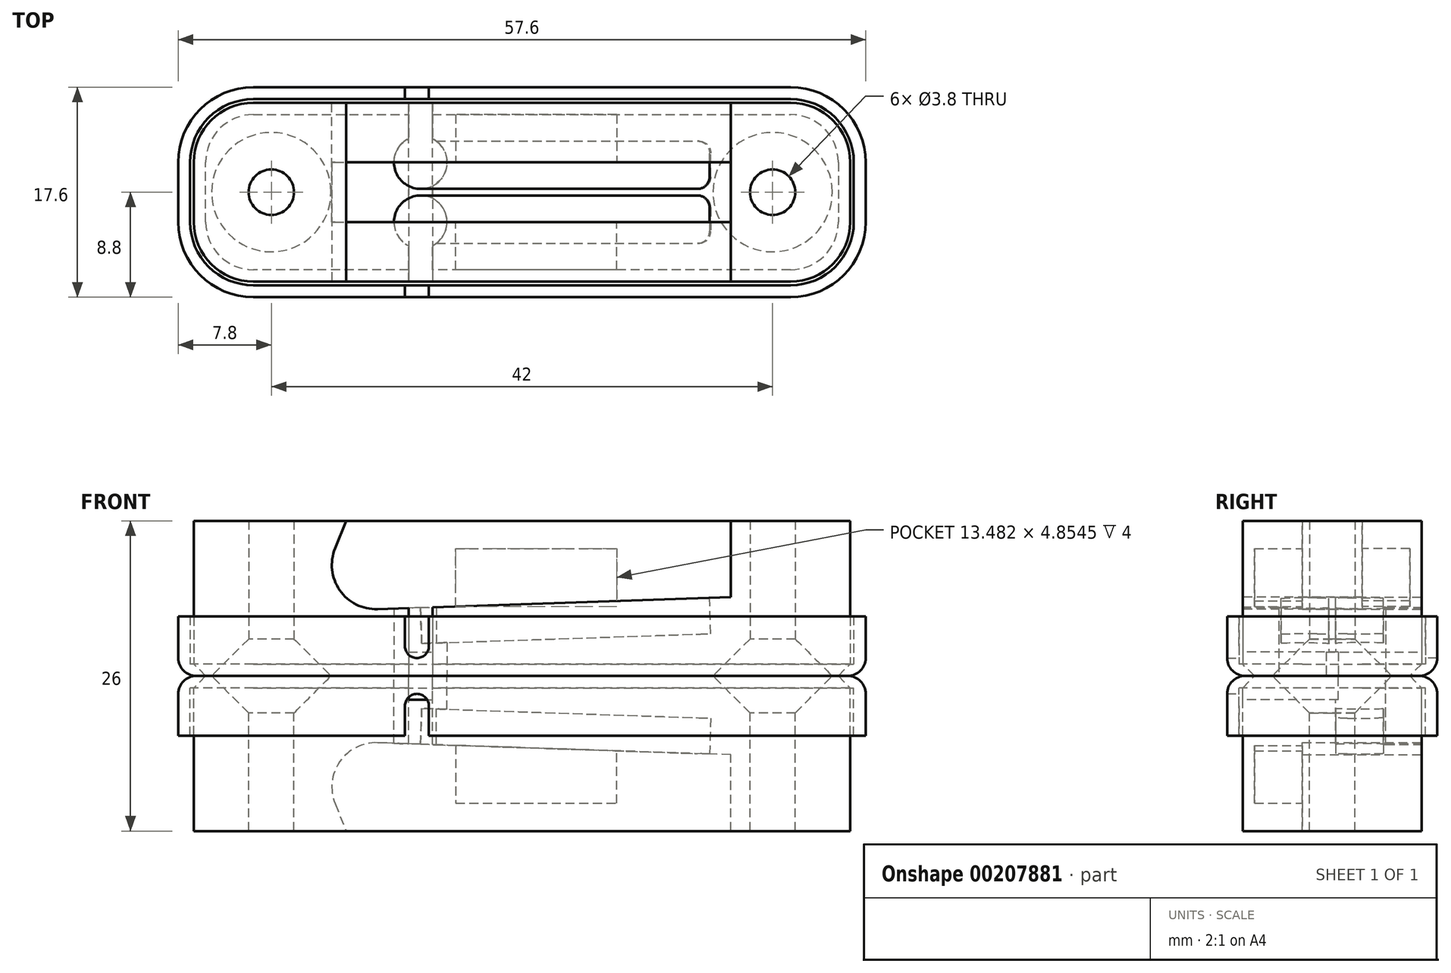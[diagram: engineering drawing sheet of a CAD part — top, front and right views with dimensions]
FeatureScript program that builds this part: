
annotation { "Feature Type Name" : "Feature", "Feature Type Description" : "" }
export const myFeature = defineFeature(function(context is Context, id is Id, definition is map)
    precondition{}
    {
        {
            var Q0;
            Q0=qCreatedBy(makeId("Top.planeOp"),FACE);
            var sketch = newSketch(context, id + "F0", { "sketchPlane" : qUnion([Q0])});
            skLineSegment(sketch, "E0.bottom", {"start": v(-22.5, 7.5) * mm, "end": v(22.5, 7.5) * mm});
            skLineSegment(sketch, "E0.top", {"start": v(-22.5, -7.5) * mm, "end": v(22.5, -7.5) * mm});
            skLineSegment(sketch, "E0.left", {"start": v(-27.5, 2.5) * mm, "end": v(-27.5, -2.5) * mm});
            skLineSegment(sketch, "E0.right", {"start": v(27.5, 2.5) * mm, "end": v(27.5, -2.5) * mm});
            skPoint(sketch, "E1", {"position": v(0, 7.5) * mm});
            skPoint(sketch, "E2", {"position": v(27.5, 0) * mm});
            skPoint(sketch, "E3.visualSharp", {"position": v(-27.5, 7.5) * mm});
            skArc(sketch, "E3.filletArc", {"start": v(-22.5, 7.5) * mm, "mid": v(-26.04, 6.04) * mm, "end": v(-27.5, 2.5) * mm});
            skPoint(sketch, "E4.visualSharp", {"position": v(27.5, 7.5) * mm});
            skArc(sketch, "E4.filletArc", {"start": v(27.5, 2.5) * mm, "mid": v(26.04, 6.04) * mm, "end": v(22.5, 7.5) * mm});
            skPoint(sketch, "E5.visualSharp", {"position": v(27.5, -7.5) * mm});
            skArc(sketch, "E5.filletArc", {"start": v(22.5, -7.5) * mm, "mid": v(26.04, -6.04) * mm, "end": v(27.5, -2.5) * mm});
            skPoint(sketch, "E6.visualSharp", {"position": v(-27.5, -7.5) * mm});
            skArc(sketch, "E6.filletArc", {"start": v(-27.5, -2.5) * mm, "mid": v(-26.04, -6.04) * mm, "end": v(-22.5, -7.5) * mm});
            skPoint(sketch, "E7", {"position": v(-21, 0) * mm});
            skPoint(sketch, "E8.MirrorP", {"position": v(21, 0) * mm});
            skSolve(sketch);
        }
        {
            var Q0;
            Q0 = qSketchRegion(id + "F0", true);
            extrude(context, id + "F1", {"entities" : qUnion([Q0]), "oppositeDirection" : true, "depth" : 13 * mm});
        }
        {
            var Q0;
            Q0=sQuery(id+"F0.wireOp",VERTEX,"E7");
            var Q1;
            Q1=makeQuery(id+"F1.opExtrude","SWEPT_BODY",BODY,{"disambiguationData":[OSD([sQuery(id+"F0.wireOp",EDGE,"E0.bottom"),sQuery(id+"F0.wireOp",EDGE,"E0.top"),sQuery(id+"F0.wireOp",EDGE,"E0.left"),sQuery(id+"F0.wireOp",EDGE,"E0.right"),sQuery(id+"F0.wireOp",EDGE,"E3.filletArc"),sQuery(id+"F0.wireOp",EDGE,"E4.filletArc"),sQuery(id+"F0.wireOp",EDGE,"E5.filletArc"),sQuery(id+"F0.wireOp",EDGE,"E6.filletArc")])]});
            hole(context, id + "F2", {"style" : HoleStyle.C_SINK, "endStyle" : HoleEndStyle.THROUGH, "holeDiameter" : 3.8 * mm, "cSinkDiameter" : 10 * mm, "cSinkAngle" : 90 * degree, "locations" : qUnion([Q0]), "scope" : qUnion([Q1]), "tappedDepth" : 12 * mm, "tapClearance" : 3});
        }
        {
            var Q0;
            Q0=sQuery(id+"F0.wireOp",VERTEX,"E8.MirrorP");
            var Q1;
            Q1=makeQuery(id+"F1.opExtrude","SWEPT_BODY",BODY,{"disambiguationData":[OSD([sQuery(id+"F0.wireOp",EDGE,"E0.bottom"),sQuery(id+"F0.wireOp",EDGE,"E0.top"),sQuery(id+"F0.wireOp",EDGE,"E0.left"),sQuery(id+"F0.wireOp",EDGE,"E0.right"),sQuery(id+"F0.wireOp",EDGE,"E3.filletArc"),sQuery(id+"F0.wireOp",EDGE,"E4.filletArc"),sQuery(id+"F0.wireOp",EDGE,"E5.filletArc"),sQuery(id+"F0.wireOp",EDGE,"E6.filletArc")])]});
            hole(context, id + "F3", {"style" : HoleStyle.C_SINK, "endStyle" : HoleEndStyle.THROUGH, "holeDiameter" : 3.8 * mm, "cSinkDiameter" : 10 * mm, "cSinkAngle" : 90 * degree, "locations" : qUnion([Q0]), "scope" : qUnion([Q1]), "tappedDepth" : 12 * mm, "tapClearance" : 3});
        }
        {
            var Q0;
            Q0=makeQuery(id+"F1.opExtrude","SWEPT_FACE",FACE,{"disambiguationData":[OSD([sQuery(id+"F0.wireOp",EDGE,"E0.bottom")])]});
            var sketch = newSketch(context, id + "F4", { "sketchPlane" : qUnion([Q0])});
            skLineSegment(sketch, "E9", {"start": v(-17.5, -13) * mm, "end": v(-17.5, -6.6) * mm});
            skLineSegment(sketch, "E10", {"start": v(-17.5, -6.6) * mm, "end": v(1.23, -5.97) * mm});
            skLineSegment(sketch, "E11", {"start": v(12.1, -13) * mm, "end": v(-17.5, -13) * mm});
            skArc(sketch, "E12", {"start": v(12.1, -13) * mm, "mid": v(12.22, -13) * mm, "end": v(12.35, -13) * mm});
            skLineSegment(sketch, "E13.trimOffspring", {"start": v(2.22, -5.93) * mm, "end": v(12.1, -5.6) * mm});
            skLineSegment(sketch, "E14", {"start": v(15.65, -10.7) * mm, "end": v(14.72, -13) * mm});
            skLineSegment(sketch, "E15", {"start": v(14.72, -13) * mm, "end": v(12.1, -13) * mm});
            skArc(sketch, "E16.trimOffspring", {"start": v(15.65, -10.7) * mm, "mid": v(15.26, -7.18) * mm, "end": v(12.1, -5.6) * mm});
            skLineSegment(sketch, "E17", {"start": v(2.22, -5.93) * mm, "end": v(1.23, -5.97) * mm});
            skSolve(sketch);
        }
        {
            var Q0;
            Q0=makeQuery(id+"F4.imprint","IMPRINT",FACE,{"disambiguationData":[TD([[makeQuery(id+"F4.imprint","IMPRINT",EDGE,{"derivedFrom":sQuery(id+"F4.wireOp",EDGE,"E9")}),-1.0]])]});
            extrude(context, id + "F5", {"entities" : qUnion([Q0]), "operationType" : NewBodyOperationType.REMOVE, "oppositeDirection" : true, "depth" : 10 * mm});
        }
        {
            var Q0;
            Q0=makeQuery(id+"F0.imprint","IMPRINT",FACE,{"disambiguationData":[TD([[makeQuery(id+"F0.imprint","IMPRINT",EDGE,{"derivedFrom":sQuery(id+"F0.wireOp",EDGE,"E0.bottom")}),-1.0]])]});
            var sketch = newSketch(context, id + "F6", { "sketchPlane" : qUnion([Q0])});
            skLineSegment(sketch, "E18.bottom", {"start": v(-7.5, 7.5) * mm, "end": v(-9.5, 7.5) * mm});
            skLineSegment(sketch, "E18.left", {"start": v(-7.5, 7.5) * mm, "end": v(-7.5, 4.49) * mm});
            skLineSegment(sketch, "E18.right", {"start": v(-9.5, 7.5) * mm, "end": v(-9.5, 4.49) * mm});
            skArc(sketch, "E19", {"start": v(-9.5, 4.49) * mm, "mid": v(-8.5, 0.28) * mm, "end": v(-7.5, 4.49) * mm});
            skPoint(sketch, "E20.orphan", {"position": v(-7.5, 2.5) * mm});
            skPoint(sketch, "E21.orphan", {"position": v(-9.5, 2.5) * mm});
            skSolve(sketch);
        }
        {
            var Q0;
            Q0 = qSketchRegion(id + "F6", true);
            extrude(context, id + "F7", {"entities" : qUnion([Q0]), "operationType" : NewBodyOperationType.REMOVE, "endBound" : BoundingType.THROUGH_ALL, "oppositeDirection" : true, "depth" : 25 * mm});
        }
        {
            var Q0;
            Q0=makeQuery(id+"F0.imprint","IMPRINT",FACE,{"disambiguationData":[TD([[makeQuery(id+"F0.imprint","IMPRINT",EDGE,{"derivedFrom":sQuery(id+"F0.wireOp",EDGE,"E0.bottom")}),-1.0]])]});
            var sketch = newSketch(context, id + "F8", { "sketchPlane" : qUnion([Q0])});
            skLineSegment(sketch, "E22.bottom", {"start": v(-9.5, 7.5) * mm, "end": v(-7.5, 7.5) * mm});
            skLineSegment(sketch, "E22.top", {"start": v(-9.5, -7.5) * mm, "end": v(-7.5, -7.5) * mm});
            skLineSegment(sketch, "E22.left", {"start": v(-9.5, 7.5) * mm, "end": v(-9.5, -7.5) * mm});
            skLineSegment(sketch, "E22.right", {"start": v(-7.5, 7.5) * mm, "end": v(-7.5, -7.5) * mm});
            skSolve(sketch);
        }
        {
            var Q0;
            {var subQ0=sQuery(id+"F0.wireOp",EDGE,"E0.bottom");var subQ1=sQuery(id+"F0.wireOp",EDGE,"E3.filletArc");Q0=makeQuery(id+"F7.boolean.opBoolean","SPLIT",EDGE,{"disambiguationData":[TD([makeQuery(id+"F1.opExtrude","SWEPT_FACE",FACE,{"disambiguationData":[OSD([subQ1])]})])],"derivedFrom":makeQuery(id+"F1.opExtrude","CAP_EDGE",EDGE,{"disambiguationData":[OSD([subQ0])],"isStart":true})});}
            chamfer(context, id + "F9", {"entities" : qUnion([Q0]), "width" : 1 * mm, "tangentPropagation" : true});
        }
        {
            var Q0;
            Q0=makeQuery(id+"F5.boolean.opBoolean","COPY",FACE,{"derivedFrom":makeQuery(id+"F5.opExtrude","SWEPT_FACE",FACE,{"disambiguationData":[OSD([sQuery(id+"F4.wireOp",EDGE,"E10"),sQuery(id+"F4.wireOp",EDGE,"E13.trimOffspring"),sQuery(id+"F4.wireOp",EDGE,"E17")])]})});
            var sketch = newSketch(context, id + "F10", { "sketchPlane" : qUnion([Q0])});
            skCircle(sketch, "E23", {"center": v(-8.3, -2.5) * mm, "radius": 2.02 * mm});
            skSolve(sketch);
        }
        {
            var Q0;
            Q0 = qSketchRegion(id + "F10", true);
            extrude(context, id + "F11", {"entities" : qUnion([Q0]), "operationType" : NewBodyOperationType.REMOVE, "oppositeDirection" : true, "depth" : 2 * mm});
        }
        {
            var Q0;
            Q0=makeQuery(id+"F5.boolean.opBoolean","COPY",FACE,{"derivedFrom":makeQuery(id+"F5.opExtrude","CAP_FACE",FACE,{"disambiguationData":[OSD([sQuery(id+"F4.wireOp",EDGE,"E9"),sQuery(id+"F4.wireOp",EDGE,"E10"),sQuery(id+"F4.wireOp",EDGE,"E11"),sQuery(id+"F4.wireOp",EDGE,"E13.trimOffspring"),sQuery(id+"F4.wireOp",EDGE,"E14"),sQuery(id+"F4.wireOp",EDGE,"E15"),sQuery(id+"F4.wireOp",EDGE,"E16.trimOffspring"),sQuery(id+"F4.wireOp",EDGE,"E17")])],"isStart":false})});
            var sketch = newSketch(context, id + "F12", { "sketchPlane" : qUnion([Q0])});
            skLineSegment(sketch, "E24", {"start": v(-7.93, -6.28) * mm, "end": v(5.55, -5.82) * mm});
            skLineSegment(sketch, "E25", {"start": v(5.55, -5.82) * mm, "end": v(5.55, -10.68) * mm});
            skLineSegment(sketch, "E26", {"start": v(5.55, -10.68) * mm, "end": v(-7.93, -10.68) * mm});
            skLineSegment(sketch, "E27", {"start": v(-7.93, -10.68) * mm, "end": v(-7.93, -6.28) * mm});
            skSolve(sketch);
        }
        {
            var Q0;
            Q0 = qSketchRegion(id + "F12", true);
            extrude(context, id + "F13", {"entities" : qUnion([Q0]), "operationType" : NewBodyOperationType.REMOVE, "oppositeDirection" : true, "depth" : 4 * mm});
        }
        {
            var Q0;
            Q0=makeQuery(id+"F13.boolean.opBoolean","MERGE",FACE,{"derivedFrom":[makeQuery(id+"F5.boolean.opBoolean","COPY",FACE,{"derivedFrom":makeQuery(id+"F5.opExtrude","SWEPT_FACE",FACE,{"disambiguationData":[OSD([sQuery(id+"F4.wireOp",EDGE,"E10"),sQuery(id+"F4.wireOp",EDGE,"E13.trimOffspring"),sQuery(id+"F4.wireOp",EDGE,"E17")])]})}),makeQuery(id+"F13.opExtrude","SWEPT_FACE",FACE,{"disambiguationData":[OSD([sQuery(id+"F12.wireOp",EDGE,"E24")])]})]});
            var sketch = newSketch(context, id + "F14", { "sketchPlane" : qUnion([Q0])});
            skLineSegment(sketch, "E28.bottom", {"start": v(-8.3, -0.28) * mm, "end": v(14.93, -0.28) * mm});
            skLineSegment(sketch, "E28.top", {"start": v(-8.3, -4.28) * mm, "end": v(14.93, -4.28) * mm});
            skLineSegment(sketch, "E28.left", {"start": v(-8.3, -0.28) * mm, "end": v(-8.3, -4.28) * mm});
            skLineSegment(sketch, "E28.right", {"start": v(15.93, -1.28) * mm, "end": v(15.93, -3.28) * mm});
            skPoint(sketch, "E29.visualSharp", {"position": v(15.93, -4.28) * mm});
            skArc(sketch, "E29.filletArc", {"start": v(14.93, -4.28) * mm, "mid": v(15.64, -3.98) * mm, "end": v(15.93, -3.28) * mm});
            skPoint(sketch, "E30.visualSharp", {"position": v(15.93, -0.28) * mm});
            skArc(sketch, "E30.filletArc", {"start": v(15.93, -1.28) * mm, "mid": v(15.64, -0.57) * mm, "end": v(14.93, -0.28) * mm});
            skSolve(sketch);
        }
        {
            var Q0;
            Q0 = qSketchRegion(id + "F14", true);
            extrude(context, id + "F15", {"entities" : qUnion([Q0]), "operationType" : NewBodyOperationType.REMOVE, "oppositeDirection" : true, "depth" : 3 * mm});
        }
        {
            var Q0;
            Q0 = qSketchRegion(id + "F8", true);
            extrude(context, id + "F16", {"entities" : qUnion([Q0]), "operationType" : NewBodyOperationType.REMOVE, "oppositeDirection" : true, "depth" : 2 * mm});
        }
        {
            var Q0;
            Q0=makeQuery(id+"F1.opExtrude","SWEPT_BODY",BODY,{"disambiguationData":[OSD([sQuery(id+"F0.wireOp",EDGE,"E0.bottom"),sQuery(id+"F0.wireOp",EDGE,"E0.top"),sQuery(id+"F0.wireOp",EDGE,"E0.left"),sQuery(id+"F0.wireOp",EDGE,"E0.right"),sQuery(id+"F0.wireOp",EDGE,"E3.filletArc"),sQuery(id+"F0.wireOp",EDGE,"E4.filletArc"),sQuery(id+"F0.wireOp",EDGE,"E5.filletArc"),sQuery(id+"F0.wireOp",EDGE,"E6.filletArc")])]});
            var Q1;
            Q1=qCreatedBy(makeId("Top.planeOp"),FACE);
            mirror(context, id + "F17", {"entities" : qUnion([Q0]), "mirrorPlane" : qUnion([Q1])});
        }
        {
            var Q0;
            Q0=makeQuery(id+"F17.opPattern","COPY",BODY,{"derivedFrom":makeQuery(id+"F1.opExtrude","SWEPT_BODY",BODY,{"disambiguationData":[OSD([sQuery(id+"F0.wireOp",EDGE,"E0.bottom"),sQuery(id+"F0.wireOp",EDGE,"E0.top"),sQuery(id+"F0.wireOp",EDGE,"E0.left"),sQuery(id+"F0.wireOp",EDGE,"E0.right"),sQuery(id+"F0.wireOp",EDGE,"E3.filletArc"),sQuery(id+"F0.wireOp",EDGE,"E4.filletArc"),sQuery(id+"F0.wireOp",EDGE,"E5.filletArc"),sQuery(id+"F0.wireOp",EDGE,"E6.filletArc")])]}),"instanceName":"1"});
            var Q1;
            Q1=qCreatedBy(makeId("Front.planeOp"),FACE);
            mirror(context, id + "F18", {"entities" : qUnion([Q0]), "mirrorPlane" : qUnion([Q1])});
        }
        {
            var Q0;
            Q0=makeQuery(id+"F0.imprint","IMPRINT",FACE,{"disambiguationData":[TD([[makeQuery(id+"F0.imprint","IMPRINT",EDGE,{"derivedFrom":sQuery(id+"F0.wireOp",EDGE,"E0.bottom")}),-1.0]])]});
            var sketch = newSketch(context, id + "F19", { "sketchPlane" : qUnion([Q0])});
            skLineSegment(sketch, "E31.0", {"start": v(-28.8, 2.5) * mm, "end": v(-28.8, -2.5) * mm});
            skArc(sketch, "E31.1", {"start": v(-22.5, 8.8) * mm, "mid": v(-26.95, 6.95) * mm, "end": v(-28.8, 2.5) * mm});
            skArc(sketch, "E31.2", {"start": v(-28.8, -2.5) * mm, "mid": v(-26.95, -6.95) * mm, "end": v(-22.5, -8.8) * mm});
            skLineSegment(sketch, "E31.3", {"start": v(22.5, 8.8) * mm, "end": v(-22.5, 8.8) * mm});
            skLineSegment(sketch, "E31.4", {"start": v(-22.5, -8.8) * mm, "end": v(22.5, -8.8) * mm});
            skArc(sketch, "E31.5", {"start": v(22.5, -8.8) * mm, "mid": v(26.95, -6.95) * mm, "end": v(28.8, -2.5) * mm});
            skLineSegment(sketch, "E31.6", {"start": v(28.8, -2.5) * mm, "end": v(28.8, 2.5) * mm});
            skArc(sketch, "E31.7", {"start": v(28.8, 2.5) * mm, "mid": v(26.95, 6.95) * mm, "end": v(22.5, 8.8) * mm});
            skSolve(sketch);
        }
        {
            var Q0;
            Q0 = qSketchRegion(id + "F19", true);
            extrude(context, id + "F20", {"entities" : qUnion([Q0]), "oppositeDirection" : true, "depth" : 5 * mm});
        }
        {
            var Q0;
            Q0=makeQuery(id+"F20.opExtrude","CAP_FACE",FACE,{"disambiguationData":[OSD([sQuery(id+"F19.wireOp",EDGE,"E31.0"),sQuery(id+"F19.wireOp",EDGE,"E31.1"),sQuery(id+"F19.wireOp",EDGE,"E31.2"),sQuery(id+"F19.wireOp",EDGE,"E31.3"),sQuery(id+"F19.wireOp",EDGE,"E31.4"),sQuery(id+"F19.wireOp",EDGE,"E31.5"),sQuery(id+"F19.wireOp",EDGE,"E31.6"),sQuery(id+"F19.wireOp",EDGE,"E31.7")])],"isStart":false});
            shell(context, id + "F21", {"entities" : qUnion([Q0]), "thickness" : 1 * mm});
        }
        {
            var Q0;
            Q0=makeQuery(id+"F20.opExtrude","SWEPT_FACE",FACE,{"disambiguationData":[OSD([sQuery(id+"F19.wireOp",EDGE,"E31.4")])]});
            var sketch = newSketch(context, id + "F22", { "sketchPlane" : qUnion([Q0])});
            skLineSegment(sketch, "E32.bottom", {"start": v(-9.8, -5) * mm, "end": v(-7.8, -5) * mm});
            skLineSegment(sketch, "E32.top", {"start": v(-9.8, -1.5) * mm, "end": v(-7.8, -1.5) * mm});
            skLineSegment(sketch, "E32.left", {"start": v(-9.8, -5) * mm, "end": v(-9.8, -1.5) * mm});
            skLineSegment(sketch, "E32.right", {"start": v(-7.8, -5) * mm, "end": v(-7.8, -1.5) * mm});
            skSolve(sketch);
        }
        {
            var Q0;
            Q0 = qSketchRegion(id + "F22", true);
            extrude(context, id + "F23", {"entities" : qUnion([Q0]), "operationType" : NewBodyOperationType.REMOVE, "endBound" : BoundingType.UP_TO_NEXT, "oppositeDirection" : true, "depth" : 25 * mm});
        }
        {
            var Q0;
            Q0=makeQuery(id+"F23.boolean.opBoolean","COPY",EDGE,{"derivedFrom":makeQuery(id+"F23.opExtrude","SWEPT_EDGE",EDGE,{"disambiguationData":[OSD([sQuery(id+"F19.wireOp",EDGE,"E31.4"),sQuery(id+"F22.wireOp",EDGE,"E32.bottom"),sQuery(id+"F22.wireOp",EDGE,"E32.left")])]})});
            var Q1;
            Q1=makeQuery(id+"F23.boolean.opBoolean","COPY",EDGE,{"derivedFrom":makeQuery(id+"F23.opExtrude","SWEPT_EDGE",EDGE,{"disambiguationData":[OSD([sQuery(id+"F19.wireOp",EDGE,"E31.4"),sQuery(id+"F22.wireOp",EDGE,"E32.bottom"),sQuery(id+"F22.wireOp",EDGE,"E32.right")])]})});
            var Q2;
            Q2=makeQuery(id+"F23.boolean.opBoolean","COPY",EDGE,{"derivedFrom":makeQuery(id+"F23.opExtrude","SWEPT_EDGE",EDGE,{"disambiguationData":[OSD([sQuery(id+"F19.wireOp",EDGE,"E31.4"),sQuery(id+"F22.wireOp",EDGE,"E32.top"),sQuery(id+"F22.wireOp",EDGE,"E32.left")])]})});
            var Q3;
            Q3=makeQuery(id+"F23.boolean.opBoolean","COPY",EDGE,{"derivedFrom":makeQuery(id+"F23.opExtrude","SWEPT_EDGE",EDGE,{"disambiguationData":[OSD([sQuery(id+"F19.wireOp",EDGE,"E31.4"),sQuery(id+"F22.wireOp",EDGE,"E32.top"),sQuery(id+"F22.wireOp",EDGE,"E32.right")])]})});
            fillet(context, id + "F24", {"entities" : qUnion([Q0, Q1, Q2, Q3]), "radius" : 1 * mm, "tangentPropagation" : true, "allowEdgeOverflow" : false});
        }
        {
            var Q0;
            Q0=makeQuery(id+"F20.opExtrude","CAP_EDGE",EDGE,{"disambiguationData":[OSD([sQuery(id+"F19.wireOp",EDGE,"E31.4")])],"isStart":true});
            fillet(context, id + "F25", {"entities" : qUnion([Q0]), "radius" : 1.5 * mm, "tangentPropagation" : true, "allowEdgeOverflow" : false});
        }
        {
            var Q0;
            Q0=makeQuery(id+"F20.opExtrude","SWEPT_BODY",BODY,{"disambiguationData":[OSD([sQuery(id+"F19.wireOp",EDGE,"E31.0"),sQuery(id+"F19.wireOp",EDGE,"E31.1"),sQuery(id+"F19.wireOp",EDGE,"E31.2"),sQuery(id+"F19.wireOp",EDGE,"E31.3"),sQuery(id+"F19.wireOp",EDGE,"E31.4"),sQuery(id+"F19.wireOp",EDGE,"E31.5"),sQuery(id+"F19.wireOp",EDGE,"E31.6"),sQuery(id+"F19.wireOp",EDGE,"E31.7")])]});
            var Q1;
            Q1=qCreatedBy(makeId("Top.planeOp"),FACE);
            mirror(context, id + "F26", {"entities" : qUnion([Q0]), "mirrorPlane" : qUnion([Q1])});
        }
        {
            var Q0;
            Q0=makeQuery(id+"F26.opPattern","COPY",BODY,{"derivedFrom":makeQuery(id+"F20.opExtrude","SWEPT_BODY",BODY,{"disambiguationData":[OSD([sQuery(id+"F19.wireOp",EDGE,"E31.0"),sQuery(id+"F19.wireOp",EDGE,"E31.1"),sQuery(id+"F19.wireOp",EDGE,"E31.2"),sQuery(id+"F19.wireOp",EDGE,"E31.3"),sQuery(id+"F19.wireOp",EDGE,"E31.4"),sQuery(id+"F19.wireOp",EDGE,"E31.5"),sQuery(id+"F19.wireOp",EDGE,"E31.6"),sQuery(id+"F19.wireOp",EDGE,"E31.7")])]}),"instanceName":"1"});
            var Q1;
            Q1=qCreatedBy(makeId("Front.planeOp"),FACE);
            mirror(context, id + "F27", {"entities" : qUnion([Q0]), "mirrorPlane" : qUnion([Q1])});
        }
    });
